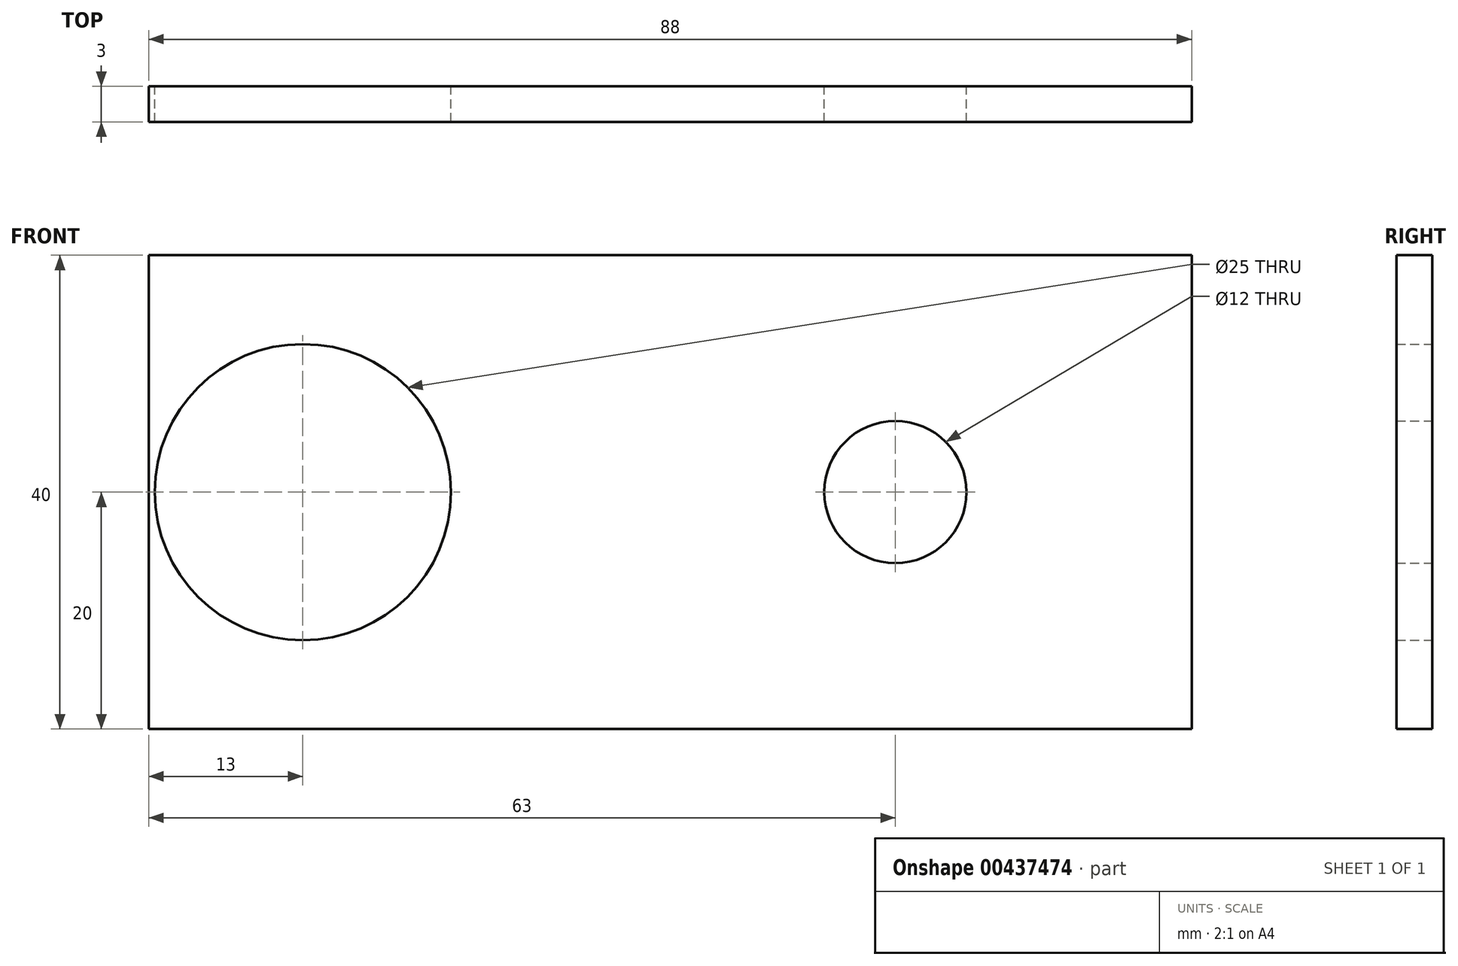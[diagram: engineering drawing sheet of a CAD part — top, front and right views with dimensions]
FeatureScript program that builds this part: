
annotation { "Feature Type Name" : "Feature", "Feature Type Description" : "" }
export const myFeature = defineFeature(function(context is Context, id is Id, definition is map)
    precondition{}
    {
        {
            var Q0;
            Q0=qCreatedBy(makeId("Front.planeOp"),FACE);
            var sketch = newSketch(context, id + "F0", { "sketchPlane" : qUnion([Q0])});
            skLineSegment(sketch, "E0.bottom", {"start": v(44, -20) * mm, "end": v(-44, -20) * mm});
            skLineSegment(sketch, "E0.top", {"start": v(44, 20) * mm, "end": v(-44, 20) * mm});
            skLineSegment(sketch, "E0.left", {"start": v(44, -20) * mm, "end": v(44, 20) * mm});
            skLineSegment(sketch, "E0.right", {"start": v(-44, -20) * mm, "end": v(-44, 20) * mm});
            skPoint(sketch, "E0.middle", {"position": v(0, 0) * mm});
            skCircle(sketch, "E1", {"center": v(-31, 0) * mm, "radius": 12.5 * mm});
            skCircle(sketch, "E2", {"center": v(19, 0) * mm, "radius": 6 * mm});
            skSolve(sketch);
        }
        {
            var Q0;
            Q0=makeQuery(id+"F0.imprint","IMPRINT",FACE,{"disambiguationData":[TD([[makeQuery(id+"F0.imprint","IMPRINT",EDGE,{"derivedFrom":sQuery(id+"F0.wireOp",EDGE,"E0.bottom")}),-1.0]])]});
            extrude(context, id + "F1", {"entities" : qUnion([Q0]), "depth" : 3 * mm, "offsetDistance" : 25 * mm});
        }
    });
